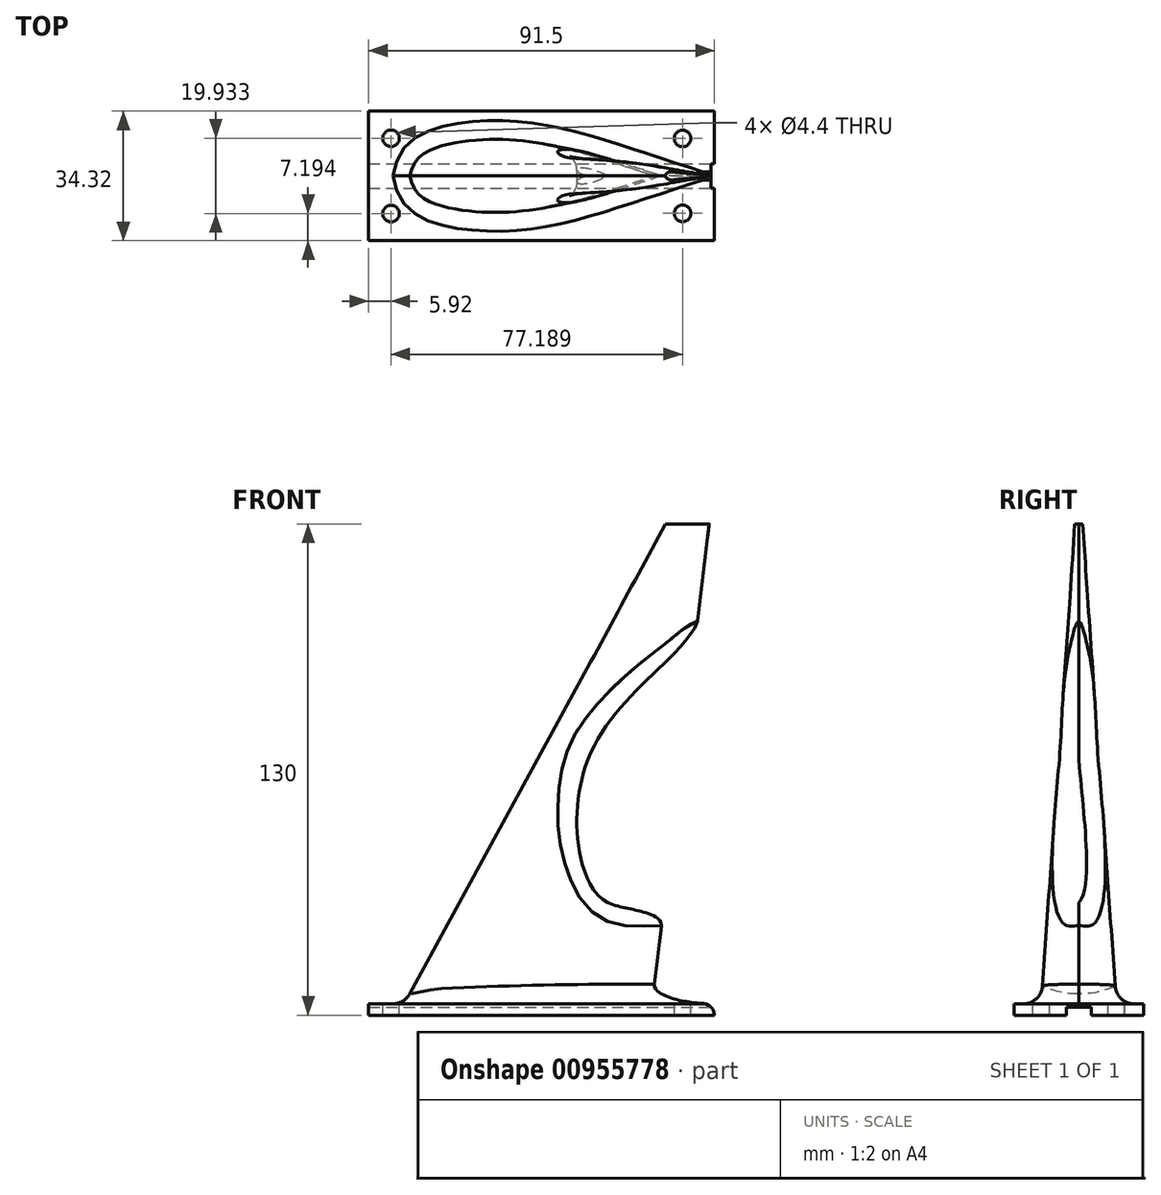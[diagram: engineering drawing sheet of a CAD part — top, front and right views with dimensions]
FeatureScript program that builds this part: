
annotation { "Feature Type Name" : "Feature", "Feature Type Description" : "" }
export const myFeature = defineFeature(function(context is Context, id is Id, definition is map)
    precondition{}
    {
        {
            var Q0;
            Q0=qCreatedBy(makeId("Top.planeOp"),FACE);
            var sketch = newSketch(context, id + "F0", { "sketchPlane" : qUnion([Q0])});
            skLineSegment(sketch, "E0", {"start": v(-28.36, 0) * mm, "end": v(38.49, 0) * mm});
            skFitSpline(sketch, "E1", {"points": [v(-28.36, 0) * mm, v(-22.92, 7.34) * mm, v(0, 10) * mm, v(38.49, 0) * mm], "startDerivative": vector(11.6, 54.73) * mm, "endDerivative": vector(109.69, -35.66) * mm});
            skFitSpline(sketch, "E2.MirrorCS", {"points": [v(-28.36, 0) * mm, v(-22.92, -7.34) * mm, v(0, -10) * mm, v(38.49, 0) * mm], "startDerivative": vector(11.6, -54.73) * mm, "endDerivative": vector(109.69, 35.66) * mm});
            skSolve(sketch);
        }
        {
            var Q0;
            Q0=qCreatedBy(makeId("Top.planeOp"),FACE);
            cPlane(context, id + "F1", {"entities" : qUnion([Q0]), "cplaneType" : CPlaneType.OFFSET, "offset" : 130 * mm, "width" : 150 * mm, "height" : 150 * mm});
        }
        {
            var Q0;
            Q0=qCreatedBy(id+"F1.planeOp",FACE);
            var sketch = newSketch(context, id + "F2", { "sketchPlane" : qUnion([Q0])});
            skFitSpline(sketch, "E3", {"points": [v(43.22, 0.93) * mm, v(45.42, 0.93) * mm, v(54, 0) * mm, v(42.5, 0) * mm, v(43.22, 0.93) * mm]});
            skLineSegment(sketch, "E4", {"start": v(42.5, 0) * mm, "end": v(54, 0) * mm});
            skFitSpline(sketch, "E5.MirrorCS", {"points": [v(43.22, -0.93) * mm, v(45.42, -0.93) * mm, v(54, 0) * mm, v(42.5, 0) * mm, v(43.22, -0.93) * mm]});
            skSolve(sketch);
        }
        {
            var Q0;
            Q0=qSketchRegion(id+"F2",true);
            var Q1;
            Q1=qSketchRegion(id+"F0",true);
            loft(context, id + "F3", {"sheetProfilesArray" : [{ "sheetProfileEntities" : qUnion([Q0]) }, { "sheetProfileEntities" : qUnion([Q1]) }]});
        }
        {
            var Q0;
            Q0=makeQuery(id+"F0.imprint","IMPRINT",FACE,{"disambiguationData":[TD([[makeQuery(id+"F0.imprint","IMPRINT",EDGE,{"derivedFrom":sQuery(id+"F0.wireOp",EDGE,"E0")}),1.0]])]});
            var sketch = newSketch(context, id + "F4", { "sketchPlane" : qUnion([Q0])});
            skLineSegment(sketch, "E6.bottom", {"start": v(-44.66, -14.97) * mm, "end": v(55.34, -14.97) * mm});
            skLineSegment(sketch, "E6.top", {"start": v(-44.66, 15.03) * mm, "end": v(55.34, 15.03) * mm});
            skLineSegment(sketch, "E6.left", {"start": v(-44.66, -14.97) * mm, "end": v(-44.66, 15.03) * mm});
            skLineSegment(sketch, "E6.right", {"start": v(55.34, -14.97) * mm, "end": v(55.34, 15.03) * mm});
            skLineSegment(sketch, "E7", {"start": v(-44.66, 0.03) * mm, "end": v(55.34, 0.03) * mm, "construction": true});
            skLineSegment(sketch, "E8", {"start": v(5.34, -14.97) * mm, "end": v(5.34, 15.03) * mm, "construction": true});
            skSolve(sketch);
        }
        {
            var Q0;
            Q0=makeQuery(id+"F6.boolean.opBoolean","MERGE",FACE,{"derivedFrom":[makeQuery(id+"F3.opLoft","CAP_FACE",FACE,{"disambiguationData":[OSD([makeQuery(id+"F0.imprint","IMPRINT",FACE,{"disambiguationData":[TD([[makeQuery(id+"F0.imprint","IMPRINT",EDGE,{"derivedFrom":sQuery(id+"F0.wireOp",EDGE,"E0")}),1.0]])]})])],"isStart":true}),makeQuery(id+"F6.opExtrude","CAP_FACE",FACE,{"disambiguationData":[OSD([sQuery(id+"F4.wireOp",EDGE,"E6.bottom"),sQuery(id+"F4.wireOp",EDGE,"E6.top"),sQuery(id+"F4.wireOp",EDGE,"E6.left"),sQuery(id+"F4.wireOp",EDGE,"E6.right")])],"isStart":true})]});
            var sketch = newSketch(context, id + "F5", { "sketchPlane" : qUnion([Q0])});
            skLineSegment(sketch, "E9.bottom", {"start": v(-44.68, 12) * mm, "end": v(-29.68, 12) * mm});
            skLineSegment(sketch, "E9.top", {"start": v(-44.68, 20) * mm, "end": v(-29.68, 20) * mm});
            skLineSegment(sketch, "E9.left", {"start": v(-44.68, 12) * mm, "end": v(-44.68, 20) * mm});
            skLineSegment(sketch, "E9.right", {"start": v(-29.68, 12) * mm, "end": v(-29.68, 20) * mm});
            skLineSegment(sketch, "E10.bottom", {"start": v(-44.68, -12) * mm, "end": v(-29.68, -12) * mm});
            skLineSegment(sketch, "E10.top", {"start": v(-44.68, -20) * mm, "end": v(-29.68, -20) * mm});
            skLineSegment(sketch, "E10.left", {"start": v(-44.68, -12) * mm, "end": v(-44.68, -20) * mm});
            skLineSegment(sketch, "E10.right", {"start": v(-29.68, -12) * mm, "end": v(-29.68, -20) * mm});
            skLineSegment(sketch, "E11", {"start": v(-29.68, 12) * mm, "end": v(-29.68, -12) * mm, "construction": true});
            skLineSegment(sketch, "E12.bottom", {"start": v(55.32, 12) * mm, "end": v(40.32, 12) * mm});
            skLineSegment(sketch, "E12.top", {"start": v(55.32, 20) * mm, "end": v(40.32, 20) * mm});
            skLineSegment(sketch, "E12.left", {"start": v(55.32, 12) * mm, "end": v(55.32, 20) * mm});
            skLineSegment(sketch, "E12.right", {"start": v(40.32, 12) * mm, "end": v(40.32, 20) * mm});
            skLineSegment(sketch, "E13.bottom", {"start": v(55.32, -12) * mm, "end": v(40.32, -12) * mm});
            skLineSegment(sketch, "E13.top", {"start": v(55.32, -20) * mm, "end": v(40.32, -20) * mm});
            skLineSegment(sketch, "E13.left", {"start": v(55.32, -12) * mm, "end": v(55.32, -20) * mm});
            skLineSegment(sketch, "E13.right", {"start": v(40.32, -12) * mm, "end": v(40.32, -20) * mm});
            skLineSegment(sketch, "E14", {"start": v(-37.18, 20) * mm, "end": v(-37.18, -20) * mm, "construction": true});
            skLineSegment(sketch, "E15", {"start": v(-44.68, 16) * mm, "end": v(40.32, 16) * mm, "construction": true});
            skLineSegment(sketch, "E16", {"start": v(-44.68, -16) * mm, "end": v(40.32, -16) * mm, "construction": true});
            skCircle(sketch, "E17", {"center": v(-37.18, 16) * mm, "radius": 2.2 * mm});
            skCircle(sketch, "E18", {"center": v(-37.18, -16) * mm, "radius": 2.2 * mm});
            skLineSegment(sketch, "E19", {"start": v(47.82, 20) * mm, "end": v(47.82, -20) * mm, "construction": true});
            skLineSegment(sketch, "E20", {"start": v(40.32, 16) * mm, "end": v(55.32, 16) * mm, "construction": true});
            skLineSegment(sketch, "E21", {"start": v(40.32, -16) * mm, "end": v(55.32, -16) * mm, "construction": true});
            skCircle(sketch, "E22", {"center": v(47.82, 16) * mm, "radius": 2.2 * mm});
            skCircle(sketch, "E23", {"center": v(47.82, -16) * mm, "radius": 2.2 * mm});
            skLineSegment(sketch, "E24", {"start": v(0, 16) * mm, "end": v(0, -16) * mm, "construction": true});
            skSolve(sketch);
        }
        {
            var Q0;
            Q0=qSketchRegion(id+"F4",true);
            extrude(context, id + "F6", {"entities" : qUnion([Q0]), "operationType" : NewBodyOperationType.ADD, "depth" : 3 * mm, "offsetDistance" : 25 * mm});
        }
        {
            var Q0;
            Q0=makeQuery(id+"F6.opExtrude","SWEPT_FACE",FACE,{"disambiguationData":[OSD([sQuery(id+"F4.wireOp",EDGE,"E6.top")])]});
            extrude(context, id + "F7", {"entities" : qUnion([Q0]), "operationType" : NewBodyOperationType.ADD, "depth" : 4 * mm, "offsetDistance" : 25 * mm});
        }
        {
            var Q0;
            Q0 = qSketchRegion(id + "F5", true);
            extrude(context, id + "F8", {"entities" : qUnion([Q0]), "operationType" : NewBodyOperationType.ADD, "oppositeDirection" : true, "depth" : 3 * mm, "offsetDistance" : 25 * mm});
        }
        {
            var Q0;
            Q0=qCreatedBy(makeId("Front.planeOp"),FACE);
            var sketch = newSketch(context, id + "F9", { "sketchPlane" : qUnion([Q0])});
            skFitSpline(sketch, "E25", {"points": [v(55.49, 27.74) * mm, v(25.19, 31.12) * mm, v(21.87, 67.64) * mm, v(46.79, 96.34) * mm, v(53, 100.6) * mm, v(57.62, 78.59) * mm], "startDerivative": vector(-212.63, 46.22) * mm, "endDerivative": vector(-52.55, -266.58) * mm});
            skLineSegment(sketch, "E26", {"start": v(55.49, 27.74) * mm, "end": v(57.62, 78.59) * mm});
            skSolve(sketch);
        }
        {
            var Q0;
            Q0 = qSketchRegion(id + "F9", true);
            extrude(context, id + "F10", {"entities" : qUnion([Q0]), "operationType" : NewBodyOperationType.REMOVE, "depth" : 50 * mm, "offsetDistance" : 25 * mm});
        }
        {
            var Q0;
            Q0 = qSketchRegion(id + "F9", true);
            extrude(context, id + "F11", {"entities" : qUnion([Q0]), "operationType" : NewBodyOperationType.REMOVE, "oppositeDirection" : true, "depth" : 25 * mm, "offsetDistance" : 25 * mm});
        }
        {
            var Q0;
            Q0=makeQuery(id+"F6.opExtrude","SWEPT_FACE",FACE,{"disambiguationData":[OSD([sQuery(id+"F4.wireOp",EDGE,"E6.bottom")])]});
            extrude(context, id + "F12", {"entities" : qUnion([Q0]), "operationType" : NewBodyOperationType.ADD, "depth" : 4 * mm, "offsetDistance" : 25 * mm});
        }
        {
            var Q0;
            {var subQ0=sQuery(id+"F2.wireOp",EDGE,"E5.MirrorCS");var subQ1=sQuery(id+"F2.wireOp",EDGE,"E4");var subQ2=sQuery(id+"F2.wireOp",EDGE,"E3");var subQ3=sQuery(id+"F0.wireOp",EDGE,"E2.MirrorCS");var subQ4=sQuery(id+"F0.wireOp",EDGE,"E1");var subQ5=sQuery(id+"F0.wireOp",EDGE,"E0");Q0=makeQuery(id+"F10.boolean.opBoolean","INTERSECT",EDGE,{"derivedFrom":[makeQuery(id+"F3.opLoft","SWEPT_FACE",FACE,{"disambiguationData":[OSD([subQ5,subQ4,subQ3,subQ2,subQ1,subQ0]),TDD([makeQuery(id+"F0.imprint","INTERSECT",VERTEX,{"disambiguationData":[OD(0.0)],"derivedFrom":[subQ5,subQ4,subQ3]}),makeQuery(id+"F0.imprint","INTERSECT",VERTEX,{"disambiguationData":[OD(1.0)],"derivedFrom":[subQ5,subQ4,subQ3]}),makeQuery(id+"F0.imprint","IMPRINT",EDGE,{"derivedFrom":subQ3}),makeQuery(id+"F2.imprint","INTERSECT",VERTEX,{"disambiguationData":[OD(0.0)],"derivedFrom":[subQ2,subQ1,subQ0]}),makeQuery(id+"F2.imprint","INTERSECT",VERTEX,{"disambiguationData":[OD(1.0)],"derivedFrom":[subQ2,subQ1,subQ0]}),makeQuery(id+"F2.imprint","IMPRINT",EDGE,{"derivedFrom":subQ0})])]}),makeQuery(id+"F10.opExtrude","SWEPT_FACE",FACE,{"disambiguationData":[OSD([sQuery(id+"F9.wireOp",EDGE,"E25")])]})]});}
            var Q1;
            {var subQ0=sQuery(id+"F2.wireOp",EDGE,"E3");var subQ1=sQuery(id+"F2.wireOp",EDGE,"E5.MirrorCS");var subQ2=sQuery(id+"F2.wireOp",EDGE,"E4");var subQ3=sQuery(id+"F0.wireOp",EDGE,"E1");var subQ4=sQuery(id+"F0.wireOp",EDGE,"E2.MirrorCS");var subQ5=sQuery(id+"F0.wireOp",EDGE,"E0");Q1=makeQuery(id+"F11.boolean.opBoolean","INTERSECT",EDGE,{"derivedFrom":[makeQuery(id+"F3.opLoft","SWEPT_FACE",FACE,{"disambiguationData":[OSD([subQ5,subQ3,subQ4,subQ0,subQ2,subQ1]),TDD([makeQuery(id+"F0.imprint","INTERSECT",VERTEX,{"disambiguationData":[OD(0.0)],"derivedFrom":[subQ5,subQ3,subQ4]}),makeQuery(id+"F0.imprint","INTERSECT",VERTEX,{"disambiguationData":[OD(1.0)],"derivedFrom":[subQ5,subQ3,subQ4]}),makeQuery(id+"F0.imprint","IMPRINT",EDGE,{"derivedFrom":subQ3}),makeQuery(id+"F2.imprint","INTERSECT",VERTEX,{"disambiguationData":[OD(0.0)],"derivedFrom":[subQ0,subQ2,subQ1]}),makeQuery(id+"F2.imprint","INTERSECT",VERTEX,{"disambiguationData":[OD(1.0)],"derivedFrom":[subQ0,subQ2,subQ1]}),makeQuery(id+"F2.imprint","IMPRINT",EDGE,{"derivedFrom":subQ0})])]}),makeQuery(id+"F11.opExtrude","SWEPT_FACE",FACE,{"disambiguationData":[OSD([sQuery(id+"F9.wireOp",EDGE,"E25")])]})]});}
            fillet(context, id + "F13", {"entities" : qUnion([Q0, Q1]), "radius" : 5 * mm, "tangentPropagation" : true, "allowEdgeOverflow" : false});
        }
        {
            var Q0;
            {var subQ0=sQuery(id+"F2.wireOp",EDGE,"E3");var subQ1=sQuery(id+"F2.wireOp",EDGE,"E5.MirrorCS");var subQ2=sQuery(id+"F2.wireOp",EDGE,"E4");var subQ3=sQuery(id+"F0.wireOp",EDGE,"E1");var subQ4=sQuery(id+"F0.wireOp",EDGE,"E2.MirrorCS");var subQ5=sQuery(id+"F0.wireOp",EDGE,"E0");Q0=makeQuery(id+"F6.boolean.opBoolean","INTERSECT",EDGE,{"derivedFrom":[makeQuery(id+"F3.opLoft","SWEPT_FACE",FACE,{"disambiguationData":[OSD([subQ5,subQ3,subQ4,subQ0,subQ2,subQ1]),TDD([makeQuery(id+"F0.imprint","INTERSECT",VERTEX,{"disambiguationData":[OD(0.0)],"derivedFrom":[subQ5,subQ3,subQ4]}),makeQuery(id+"F0.imprint","INTERSECT",VERTEX,{"disambiguationData":[OD(1.0)],"derivedFrom":[subQ5,subQ3,subQ4]}),makeQuery(id+"F0.imprint","IMPRINT",EDGE,{"derivedFrom":subQ3}),makeQuery(id+"F2.imprint","INTERSECT",VERTEX,{"disambiguationData":[OD(0.0)],"derivedFrom":[subQ0,subQ2,subQ1]}),makeQuery(id+"F2.imprint","INTERSECT",VERTEX,{"disambiguationData":[OD(1.0)],"derivedFrom":[subQ0,subQ2,subQ1]}),makeQuery(id+"F2.imprint","IMPRINT",EDGE,{"derivedFrom":subQ0})])]}),makeQuery(id+"F6.opExtrude","CAP_FACE",FACE,{"disambiguationData":[OSD([sQuery(id+"F4.wireOp",EDGE,"E6.bottom"),sQuery(id+"F4.wireOp",EDGE,"E6.top"),sQuery(id+"F4.wireOp",EDGE,"E6.left"),sQuery(id+"F4.wireOp",EDGE,"E6.right")])],"isStart":false})]});}
            var Q1;
            {var subQ0=sQuery(id+"F2.wireOp",EDGE,"E5.MirrorCS");var subQ1=sQuery(id+"F2.wireOp",EDGE,"E4");var subQ2=sQuery(id+"F2.wireOp",EDGE,"E3");var subQ3=sQuery(id+"F0.wireOp",EDGE,"E2.MirrorCS");var subQ4=sQuery(id+"F0.wireOp",EDGE,"E1");var subQ5=sQuery(id+"F0.wireOp",EDGE,"E0");Q1=makeQuery(id+"F6.boolean.opBoolean","INTERSECT",EDGE,{"derivedFrom":[makeQuery(id+"F3.opLoft","SWEPT_FACE",FACE,{"disambiguationData":[OSD([subQ5,subQ4,subQ3,subQ2,subQ1,subQ0]),TDD([makeQuery(id+"F0.imprint","INTERSECT",VERTEX,{"disambiguationData":[OD(0.0)],"derivedFrom":[subQ5,subQ4,subQ3]}),makeQuery(id+"F0.imprint","INTERSECT",VERTEX,{"disambiguationData":[OD(1.0)],"derivedFrom":[subQ5,subQ4,subQ3]}),makeQuery(id+"F0.imprint","IMPRINT",EDGE,{"derivedFrom":subQ3}),makeQuery(id+"F2.imprint","INTERSECT",VERTEX,{"disambiguationData":[OD(0.0)],"derivedFrom":[subQ2,subQ1,subQ0]}),makeQuery(id+"F2.imprint","INTERSECT",VERTEX,{"disambiguationData":[OD(1.0)],"derivedFrom":[subQ2,subQ1,subQ0]}),makeQuery(id+"F2.imprint","IMPRINT",EDGE,{"derivedFrom":subQ0})])]}),makeQuery(id+"F6.opExtrude","CAP_FACE",FACE,{"disambiguationData":[OSD([sQuery(id+"F4.wireOp",EDGE,"E6.bottom"),sQuery(id+"F4.wireOp",EDGE,"E6.top"),sQuery(id+"F4.wireOp",EDGE,"E6.left"),sQuery(id+"F4.wireOp",EDGE,"E6.right")])],"isStart":false})]});}
            fillet(context, id + "F14", {"entities" : qUnion([Q0, Q1]), "radius" : 5 * mm, "tangentPropagation" : true, "allowEdgeOverflow" : false});
        }
        {
            var Q0;
            Q0=makeQuery(id+"F12.boolean.opBoolean","INTERSECT",EDGE,{"derivedFrom":[makeQuery(id+"F8.opExtrude","SWEPT_FACE",FACE,{"disambiguationData":[OSD([sQuery(id+"F5.wireOp",EDGE,"E9.right")])]}),makeQuery(id+"F12.opExtrude","CAP_FACE",FACE,{"disambiguationData":[OSD([sQuery(id+"F4.wireOp",EDGE,"E6.bottom")])],"isStart":false})]});
            var Q1;
            Q1=makeQuery(id+"F12.boolean.opBoolean","INTERSECT",EDGE,{"derivedFrom":[makeQuery(id+"F8.opExtrude","SWEPT_FACE",FACE,{"disambiguationData":[OSD([sQuery(id+"F5.wireOp",EDGE,"E12.right")])]}),makeQuery(id+"F12.opExtrude","CAP_FACE",FACE,{"disambiguationData":[OSD([sQuery(id+"F4.wireOp",EDGE,"E6.bottom")])],"isStart":false})]});
            var Q2;
            Q2=makeQuery(id+"F8.boolean.opBoolean","INTERSECT",EDGE,{"derivedFrom":[makeQuery(id+"F7.opExtrude","CAP_FACE",FACE,{"disambiguationData":[OSD([sQuery(id+"F4.wireOp",EDGE,"E6.top")])],"isStart":false}),makeQuery(id+"F8.opExtrude","SWEPT_FACE",FACE,{"disambiguationData":[OSD([sQuery(id+"F5.wireOp",EDGE,"E13.right")])]})]});
            var Q3;
            Q3=makeQuery(id+"F8.boolean.opBoolean","INTERSECT",EDGE,{"derivedFrom":[makeQuery(id+"F7.opExtrude","CAP_FACE",FACE,{"disambiguationData":[OSD([sQuery(id+"F4.wireOp",EDGE,"E6.top")])],"isStart":false}),makeQuery(id+"F8.opExtrude","SWEPT_FACE",FACE,{"disambiguationData":[OSD([sQuery(id+"F5.wireOp",EDGE,"E10.right")])]})]});
            fillet(context, id + "F15", {"entities" : qUnion([Q0, Q1, Q2, Q3]), "radius" : 5 * mm, "tangentPropagation" : true, "allowEdgeOverflow" : false});
        }
        {
            var Q0;
            {var subQ0=sQuery(id+"F5.wireOp",EDGE,"E17");var subQ1=sQuery(id+"F5.wireOp",EDGE,"E9.right");var subQ2=makeQuery(id+"F8.opExtrude","CAP_FACE",FACE,{"disambiguationData":[OSD([sQuery(id+"F5.wireOp",EDGE,"E9.bottom"),sQuery(id+"F5.wireOp",EDGE,"E9.top"),sQuery(id+"F5.wireOp",EDGE,"E9.left"),subQ1,subQ0])],"isStart":false});var subQ3=sQuery(id+"F4.wireOp",EDGE,"E6.right");var subQ4=sQuery(id+"F4.wireOp",EDGE,"E6.top");var subQ5=sQuery(id+"F4.wireOp",EDGE,"E6.bottom");var subQ6=makeQuery(id+"F6.opExtrude","CAP_FACE",FACE,{"disambiguationData":[OSD([subQ5,subQ4,sQuery(id+"F4.wireOp",EDGE,"E6.left"),subQ3])],"isStart":false});var subQ7=makeQuery(id+"F7.opExtrude","SWEPT_FACE",FACE,{"disambiguationData":[OSD([subQ4]),TDD([makeQuery(id+"F6.opExtrude","CAP_EDGE",EDGE,{"disambiguationData":[OSD([subQ4])],"isStart":false})])]});var subQ9=makeQuery(id+"F8.opExtrude","CAP_FACE",FACE,{"disambiguationData":[OSD([sQuery(id+"F5.wireOp",EDGE,"E13.bottom"),sQuery(id+"F5.wireOp",EDGE,"E13.top"),sQuery(id+"F5.wireOp",EDGE,"E13.left"),sQuery(id+"F5.wireOp",EDGE,"E13.right"),sQuery(id+"F5.wireOp",EDGE,"E23")])],"isStart":false});var subQ10=makeQuery(id+"F8.opExtrude","CAP_FACE",FACE,{"disambiguationData":[OSD([sQuery(id+"F5.wireOp",EDGE,"E10.bottom"),sQuery(id+"F5.wireOp",EDGE,"E10.top"),sQuery(id+"F5.wireOp",EDGE,"E10.left"),sQuery(id+"F5.wireOp",EDGE,"E10.right"),sQuery(id+"F5.wireOp",EDGE,"E18")])],"isStart":false});var subQ11=sQuery(id+"F5.wireOp",EDGE,"E22");var subQ12=sQuery(id+"F5.wireOp",EDGE,"E12.right");var subQ13=sQuery(id+"F5.wireOp",EDGE,"E12.left");var subQ14=makeQuery(id+"F8.opExtrude","CAP_FACE",FACE,{"disambiguationData":[OSD([sQuery(id+"F5.wireOp",EDGE,"E12.bottom"),sQuery(id+"F5.wireOp",EDGE,"E12.top"),subQ13,subQ12,subQ11])],"isStart":false});var subQ15=makeQuery(id+"F6.opExtrude","CAP_EDGE",EDGE,{"disambiguationData":[OSD([subQ5])],"isStart":false});Q0=makeQuery(id+"F12.boolean.opBoolean","MERGE",FACE,{"derivedFrom":[makeQuery(id+"F8.boolean.opBoolean","MERGE",FACE,{"derivedFrom":[makeQuery(id+"F7.boolean.opBoolean","MERGE",FACE,{"derivedFrom":[subQ6,subQ7]}),subQ2,subQ10,subQ14,subQ9]}),makeQuery(id+"F12.opExtrude","SWEPT_FACE",FACE,{"disambiguationData":[OSD([subQ5]),TDD([makeQuery(id+"F8.boolean.opBoolean","SPLIT",EDGE,{"disambiguationData":[TD([makeQuery(id+"F6.opExtrude","SWEPT_FACE",FACE,{"disambiguationData":[OSD([subQ3])]})])],"derivedFrom":subQ15})])]}),makeQuery(id+"F12.opExtrude","SWEPT_FACE",FACE,{"disambiguationData":[OSD([subQ5]),TDD([makeQuery(id+"F8.boolean.opBoolean","SPLIT",EDGE,{"disambiguationData":[TD([makeQuery(id+"F8.opExtrude","SWEPT_FACE",FACE,{"disambiguationData":[OSD([subQ1])]})])],"derivedFrom":subQ15})])]}),makeQuery(id+"F12.opExtrude","SWEPT_FACE",FACE,{"disambiguationData":[OSD([subQ5]),TDD([makeQuery(id+"F8.boolean.opBoolean","SPLIT",EDGE,{"disambiguationData":[TD([makeQuery(id+"F8.opExtrude","SWEPT_FACE",FACE,{"disambiguationData":[OSD([subQ0])]})])],"derivedFrom":subQ15})])]}),makeQuery(id+"F12.opExtrude","SWEPT_FACE",FACE,{"disambiguationData":[OSD([subQ5]),TDD([makeQuery(id+"F8.boolean.opBoolean","SPLIT",EDGE,{"disambiguationData":[TD([makeQuery(id+"F8.opExtrude","SWEPT_FACE",FACE,{"disambiguationData":[OSD([subQ11])]})])],"derivedFrom":subQ15})])]})]});}
            var sketch = newSketch(context, id + "F16", { "sketchPlane" : qUnion([Q0])});
            skLineSegment(sketch, "E27.bottom", {"start": v(-44.68, 20) * mm, "end": v(55.32, 20) * mm});
            skLineSegment(sketch, "E27.top", {"start": v(-44.68, -20) * mm, "end": v(55.32, -20) * mm});
            skLineSegment(sketch, "E27.left", {"start": v(-44.68, 20) * mm, "end": v(-44.68, -20) * mm});
            skLineSegment(sketch, "E27.right", {"start": v(55.32, 20) * mm, "end": v(55.32, -20) * mm});
            skSolve(sketch);
        }
        {
            var Q0;
            Q0 = qSketchRegion(id + "F16", true);
            var Q1;
            {var subQ0=sQuery(id+"F4.wireOp",EDGE,"E6.top");var subQ1=makeQuery(id+"F7.opExtrude","SWEPT_FACE",FACE,{"disambiguationData":[OSD([subQ0]),TDD([makeQuery(id+"F6.opExtrude","CAP_EDGE",EDGE,{"disambiguationData":[OSD([subQ0])],"isStart":true})])]});var subQ2=makeQuery(id+"F8.opExtrude","CAP_FACE",FACE,{"disambiguationData":[OSD([sQuery(id+"F5.wireOp",EDGE,"E13.bottom"),sQuery(id+"F5.wireOp",EDGE,"E13.top"),sQuery(id+"F5.wireOp",EDGE,"E13.left"),sQuery(id+"F5.wireOp",EDGE,"E13.right"),sQuery(id+"F5.wireOp",EDGE,"E23")])],"isStart":true});var subQ3=sQuery(id+"F4.wireOp",EDGE,"E6.right");var subQ4=sQuery(id+"F4.wireOp",EDGE,"E6.bottom");var subQ5=makeQuery(id+"F6.opExtrude","CAP_FACE",FACE,{"disambiguationData":[OSD([subQ4,subQ0,sQuery(id+"F4.wireOp",EDGE,"E6.left"),subQ3])],"isStart":true});var subQ7=makeQuery(id+"F0.imprint","IMPRINT",EDGE,{"derivedFrom":sQuery(id+"F0.wireOp",EDGE,"E0")});var subQ8=makeQuery(id+"F3.opLoft","CAP_FACE",FACE,{"disambiguationData":[OSD([makeQuery(id+"F0.imprint","IMPRINT",FACE,{"disambiguationData":[TD([[subQ7,1.0]])]}),makeQuery(id+"F0.imprint","IMPRINT",FACE,{"disambiguationData":[TD([[subQ7,-1.0]])]})])],"isStart":true});var subQ9=sQuery(id+"F5.wireOp",EDGE,"E22");var subQ10=sQuery(id+"F5.wireOp",EDGE,"E12.right");var subQ11=sQuery(id+"F5.wireOp",EDGE,"E12.left");var subQ12=makeQuery(id+"F8.opExtrude","CAP_FACE",FACE,{"disambiguationData":[OSD([sQuery(id+"F5.wireOp",EDGE,"E12.bottom"),sQuery(id+"F5.wireOp",EDGE,"E12.top"),subQ11,subQ10,subQ9])],"isStart":true});var subQ13=sQuery(id+"F5.wireOp",EDGE,"E17");var subQ14=sQuery(id+"F5.wireOp",EDGE,"E9.right");var subQ15=makeQuery(id+"F8.opExtrude","CAP_FACE",FACE,{"disambiguationData":[OSD([sQuery(id+"F5.wireOp",EDGE,"E9.bottom"),sQuery(id+"F5.wireOp",EDGE,"E9.top"),sQuery(id+"F5.wireOp",EDGE,"E9.left"),subQ14,subQ13])],"isStart":true});var subQ16=makeQuery(id+"F8.opExtrude","CAP_FACE",FACE,{"disambiguationData":[OSD([sQuery(id+"F5.wireOp",EDGE,"E10.bottom"),sQuery(id+"F5.wireOp",EDGE,"E10.top"),sQuery(id+"F5.wireOp",EDGE,"E10.left"),sQuery(id+"F5.wireOp",EDGE,"E10.right"),sQuery(id+"F5.wireOp",EDGE,"E18")])],"isStart":true});var subQ17=makeQuery(id+"F6.opExtrude","CAP_EDGE",EDGE,{"disambiguationData":[OSD([subQ4])],"isStart":true});Q1=makeQuery(id+"F12.boolean.opBoolean","MERGE",FACE,{"derivedFrom":[makeQuery(id+"F8.boolean.opBoolean","MERGE",FACE,{"derivedFrom":[makeQuery(id+"F7.boolean.opBoolean","MERGE",FACE,{"derivedFrom":[makeQuery(id+"F6.boolean.opBoolean","MERGE",FACE,{"derivedFrom":[subQ8,subQ5]}),subQ1]}),subQ15,subQ16,subQ12,subQ2]}),makeQuery(id+"F12.opExtrude","SWEPT_FACE",FACE,{"disambiguationData":[OSD([subQ4]),TDD([makeQuery(id+"F8.boolean.opBoolean","SPLIT",EDGE,{"disambiguationData":[TD([makeQuery(id+"F6.opExtrude","SWEPT_FACE",FACE,{"disambiguationData":[OSD([subQ3])]})])],"derivedFrom":subQ17})])]}),makeQuery(id+"F12.opExtrude","SWEPT_FACE",FACE,{"disambiguationData":[OSD([subQ4]),TDD([makeQuery(id+"F8.boolean.opBoolean","SPLIT",EDGE,{"disambiguationData":[TD([makeQuery(id+"F8.opExtrude","SWEPT_FACE",FACE,{"disambiguationData":[OSD([subQ14])]})])],"derivedFrom":subQ17})])]}),makeQuery(id+"F12.opExtrude","SWEPT_FACE",FACE,{"disambiguationData":[OSD([subQ4]),TDD([makeQuery(id+"F8.boolean.opBoolean","SPLIT",EDGE,{"disambiguationData":[TD([makeQuery(id+"F8.opExtrude","SWEPT_FACE",FACE,{"disambiguationData":[OSD([subQ13])]})])],"derivedFrom":subQ17})])]}),makeQuery(id+"F12.opExtrude","SWEPT_FACE",FACE,{"disambiguationData":[OSD([subQ4]),TDD([makeQuery(id+"F8.boolean.opBoolean","SPLIT",EDGE,{"disambiguationData":[TD([makeQuery(id+"F8.opExtrude","SWEPT_FACE",FACE,{"disambiguationData":[OSD([subQ9])]})])],"derivedFrom":subQ17})])]})]});}
            extrude(context, id + "F17", {"entities" : qUnion([Q0]), "operationType" : NewBodyOperationType.ADD, "endBound" : BoundingType.UP_TO_SURFACE, "oppositeDirection" : true, "depth" : 25 * mm, "endBoundEntityFace" : qUnion([Q1]), "offsetDistance" : 25 * mm});
        }
        {
            var Q0;
            {var subQ0=sQuery(id+"F5.wireOp",EDGE,"E17");var subQ1=sQuery(id+"F5.wireOp",EDGE,"E9.right");var subQ2=makeQuery(id+"F8.opExtrude","CAP_FACE",FACE,{"disambiguationData":[OSD([sQuery(id+"F5.wireOp",EDGE,"E9.bottom"),sQuery(id+"F5.wireOp",EDGE,"E9.top"),sQuery(id+"F5.wireOp",EDGE,"E9.left"),subQ1,subQ0])],"isStart":false});var subQ3=sQuery(id+"F4.wireOp",EDGE,"E6.right");var subQ4=sQuery(id+"F4.wireOp",EDGE,"E6.top");var subQ5=sQuery(id+"F4.wireOp",EDGE,"E6.bottom");var subQ6=makeQuery(id+"F6.opExtrude","CAP_FACE",FACE,{"disambiguationData":[OSD([subQ5,subQ4,sQuery(id+"F4.wireOp",EDGE,"E6.left"),subQ3])],"isStart":false});var subQ7=makeQuery(id+"F7.opExtrude","SWEPT_FACE",FACE,{"disambiguationData":[OSD([subQ4]),TDD([makeQuery(id+"F6.opExtrude","CAP_EDGE",EDGE,{"disambiguationData":[OSD([subQ4])],"isStart":false})])]});var subQ9=makeQuery(id+"F8.opExtrude","CAP_FACE",FACE,{"disambiguationData":[OSD([sQuery(id+"F5.wireOp",EDGE,"E13.bottom"),sQuery(id+"F5.wireOp",EDGE,"E13.top"),sQuery(id+"F5.wireOp",EDGE,"E13.left"),sQuery(id+"F5.wireOp",EDGE,"E13.right"),sQuery(id+"F5.wireOp",EDGE,"E23")])],"isStart":false});var subQ10=makeQuery(id+"F8.opExtrude","CAP_FACE",FACE,{"disambiguationData":[OSD([sQuery(id+"F5.wireOp",EDGE,"E10.bottom"),sQuery(id+"F5.wireOp",EDGE,"E10.top"),sQuery(id+"F5.wireOp",EDGE,"E10.left"),sQuery(id+"F5.wireOp",EDGE,"E10.right"),sQuery(id+"F5.wireOp",EDGE,"E18")])],"isStart":false});var subQ11=sQuery(id+"F5.wireOp",EDGE,"E22");var subQ12=sQuery(id+"F5.wireOp",EDGE,"E12.right");var subQ13=sQuery(id+"F5.wireOp",EDGE,"E12.left");var subQ14=makeQuery(id+"F8.opExtrude","CAP_FACE",FACE,{"disambiguationData":[OSD([sQuery(id+"F5.wireOp",EDGE,"E12.bottom"),sQuery(id+"F5.wireOp",EDGE,"E12.top"),subQ13,subQ12,subQ11])],"isStart":false});var subQ15=makeQuery(id+"F6.opExtrude","CAP_EDGE",EDGE,{"disambiguationData":[OSD([subQ5])],"isStart":false});Q0=makeQuery(id+"F17.boolean.opBoolean","MERGE",FACE,{"derivedFrom":[makeQuery(id+"F12.boolean.opBoolean","MERGE",FACE,{"derivedFrom":[makeQuery(id+"F8.boolean.opBoolean","MERGE",FACE,{"derivedFrom":[makeQuery(id+"F7.boolean.opBoolean","MERGE",FACE,{"derivedFrom":[subQ6,subQ7]}),subQ2,subQ10,subQ14,subQ9]}),makeQuery(id+"F12.opExtrude","SWEPT_FACE",FACE,{"disambiguationData":[OSD([subQ5]),TDD([makeQuery(id+"F8.boolean.opBoolean","SPLIT",EDGE,{"disambiguationData":[TD([makeQuery(id+"F6.opExtrude","SWEPT_FACE",FACE,{"disambiguationData":[OSD([subQ3])]})])],"derivedFrom":subQ15})])]}),makeQuery(id+"F12.opExtrude","SWEPT_FACE",FACE,{"disambiguationData":[OSD([subQ5]),TDD([makeQuery(id+"F8.boolean.opBoolean","SPLIT",EDGE,{"disambiguationData":[TD([makeQuery(id+"F8.opExtrude","SWEPT_FACE",FACE,{"disambiguationData":[OSD([subQ1])]})])],"derivedFrom":subQ15})])]}),makeQuery(id+"F12.opExtrude","SWEPT_FACE",FACE,{"disambiguationData":[OSD([subQ5]),TDD([makeQuery(id+"F8.boolean.opBoolean","SPLIT",EDGE,{"disambiguationData":[TD([makeQuery(id+"F8.opExtrude","SWEPT_FACE",FACE,{"disambiguationData":[OSD([subQ0])]})])],"derivedFrom":subQ15})])]}),makeQuery(id+"F12.opExtrude","SWEPT_FACE",FACE,{"disambiguationData":[OSD([subQ5]),TDD([makeQuery(id+"F8.boolean.opBoolean","SPLIT",EDGE,{"disambiguationData":[TD([makeQuery(id+"F8.opExtrude","SWEPT_FACE",FACE,{"disambiguationData":[OSD([subQ11])]})])],"derivedFrom":subQ15})])]})]}),makeQuery(id+"F17.opExtrude","CAP_FACE",FACE,{"disambiguationData":[OSD([sQuery(id+"F16.wireOp",EDGE,"E27.bottom"),sQuery(id+"F16.wireOp",EDGE,"E27.top"),sQuery(id+"F16.wireOp",EDGE,"E27.left"),sQuery(id+"F16.wireOp",EDGE,"E27.right")])],"isStart":true})]});}
            var sketch = newSketch(context, id + "F18", { "sketchPlane" : qUnion([Q0])});
            skLineSegment(sketch, "E28.bottom", {"start": v(55.34, 17.16) * mm, "end": v(-36.16, 17.16) * mm});
            skLineSegment(sketch, "E28.top", {"start": v(55.34, -17.16) * mm, "end": v(-36.16, -17.16) * mm});
            skLineSegment(sketch, "E28.left", {"start": v(55.34, 17.16) * mm, "end": v(55.34, -17.16) * mm});
            skLineSegment(sketch, "E28.right", {"start": v(-36.16, 17.16) * mm, "end": v(-36.16, -17.16) * mm});
            skLineSegment(sketch, "E29", {"start": v(-36.16, 0) * mm, "end": v(0, 0) * mm, "construction": true});
            skLineSegment(sketch, "E30.bottom", {"start": v(-66.77, 30.67) * mm, "end": v(66.77, 30.67) * mm});
            skLineSegment(sketch, "E30.top", {"start": v(-66.77, -30.67) * mm, "end": v(66.77, -30.67) * mm});
            skLineSegment(sketch, "E30.left", {"start": v(-66.77, 30.67) * mm, "end": v(-66.77, -30.67) * mm});
            skLineSegment(sketch, "E30.right", {"start": v(66.77, 30.67) * mm, "end": v(66.77, -30.67) * mm});
            skPoint(sketch, "E30.middle", {"position": v(0, 0) * mm});
            skSolve(sketch);
        }
        {
            var Q0;
            Q0 = qSketchRegion(id + "F18", true);
            extrude(context, id + "F19", {"entities" : qUnion([Q0]), "operationType" : NewBodyOperationType.REMOVE, "oppositeDirection" : true, "depth" : 25 * mm, "offsetDistance" : 25 * mm});
        }
        {
            var Q0;
            {var subQ0=sQuery(id+"F5.wireOp",EDGE,"E17");var subQ1=sQuery(id+"F5.wireOp",EDGE,"E9.right");var subQ2=makeQuery(id+"F8.opExtrude","CAP_FACE",FACE,{"disambiguationData":[OSD([sQuery(id+"F5.wireOp",EDGE,"E9.bottom"),sQuery(id+"F5.wireOp",EDGE,"E9.top"),sQuery(id+"F5.wireOp",EDGE,"E9.left"),subQ1,subQ0])],"isStart":false});var subQ3=sQuery(id+"F4.wireOp",EDGE,"E6.right");var subQ4=sQuery(id+"F4.wireOp",EDGE,"E6.top");var subQ5=sQuery(id+"F4.wireOp",EDGE,"E6.bottom");var subQ6=makeQuery(id+"F6.opExtrude","CAP_FACE",FACE,{"disambiguationData":[OSD([subQ5,subQ4,sQuery(id+"F4.wireOp",EDGE,"E6.left"),subQ3])],"isStart":false});var subQ7=makeQuery(id+"F7.opExtrude","SWEPT_FACE",FACE,{"disambiguationData":[OSD([subQ4]),TDD([makeQuery(id+"F6.opExtrude","CAP_EDGE",EDGE,{"disambiguationData":[OSD([subQ4])],"isStart":false})])]});var subQ9=makeQuery(id+"F8.opExtrude","CAP_FACE",FACE,{"disambiguationData":[OSD([sQuery(id+"F5.wireOp",EDGE,"E13.bottom"),sQuery(id+"F5.wireOp",EDGE,"E13.top"),sQuery(id+"F5.wireOp",EDGE,"E13.left"),sQuery(id+"F5.wireOp",EDGE,"E13.right"),sQuery(id+"F5.wireOp",EDGE,"E23")])],"isStart":false});var subQ10=makeQuery(id+"F8.opExtrude","CAP_FACE",FACE,{"disambiguationData":[OSD([sQuery(id+"F5.wireOp",EDGE,"E10.bottom"),sQuery(id+"F5.wireOp",EDGE,"E10.top"),sQuery(id+"F5.wireOp",EDGE,"E10.left"),sQuery(id+"F5.wireOp",EDGE,"E10.right"),sQuery(id+"F5.wireOp",EDGE,"E18")])],"isStart":false});var subQ11=sQuery(id+"F5.wireOp",EDGE,"E22");var subQ12=sQuery(id+"F5.wireOp",EDGE,"E12.right");var subQ13=sQuery(id+"F5.wireOp",EDGE,"E12.left");var subQ14=makeQuery(id+"F8.opExtrude","CAP_FACE",FACE,{"disambiguationData":[OSD([sQuery(id+"F5.wireOp",EDGE,"E12.bottom"),sQuery(id+"F5.wireOp",EDGE,"E12.top"),subQ13,subQ12,subQ11])],"isStart":false});var subQ15=makeQuery(id+"F6.opExtrude","CAP_EDGE",EDGE,{"disambiguationData":[OSD([subQ5])],"isStart":false});Q0=makeQuery(id+"F17.boolean.opBoolean","MERGE",FACE,{"derivedFrom":[makeQuery(id+"F12.boolean.opBoolean","MERGE",FACE,{"derivedFrom":[makeQuery(id+"F8.boolean.opBoolean","MERGE",FACE,{"derivedFrom":[makeQuery(id+"F7.boolean.opBoolean","MERGE",FACE,{"derivedFrom":[subQ6,subQ7]}),subQ2,subQ10,subQ14,subQ9]}),makeQuery(id+"F12.opExtrude","SWEPT_FACE",FACE,{"disambiguationData":[OSD([subQ5]),TDD([makeQuery(id+"F8.boolean.opBoolean","SPLIT",EDGE,{"disambiguationData":[TD([makeQuery(id+"F6.opExtrude","SWEPT_FACE",FACE,{"disambiguationData":[OSD([subQ3])]})])],"derivedFrom":subQ15})])]}),makeQuery(id+"F12.opExtrude","SWEPT_FACE",FACE,{"disambiguationData":[OSD([subQ5]),TDD([makeQuery(id+"F8.boolean.opBoolean","SPLIT",EDGE,{"disambiguationData":[TD([makeQuery(id+"F8.opExtrude","SWEPT_FACE",FACE,{"disambiguationData":[OSD([subQ1])]})])],"derivedFrom":subQ15})])]}),makeQuery(id+"F12.opExtrude","SWEPT_FACE",FACE,{"disambiguationData":[OSD([subQ5]),TDD([makeQuery(id+"F8.boolean.opBoolean","SPLIT",EDGE,{"disambiguationData":[TD([makeQuery(id+"F8.opExtrude","SWEPT_FACE",FACE,{"disambiguationData":[OSD([subQ0])]})])],"derivedFrom":subQ15})])]}),makeQuery(id+"F12.opExtrude","SWEPT_FACE",FACE,{"disambiguationData":[OSD([subQ5]),TDD([makeQuery(id+"F8.boolean.opBoolean","SPLIT",EDGE,{"disambiguationData":[TD([makeQuery(id+"F8.opExtrude","SWEPT_FACE",FACE,{"disambiguationData":[OSD([subQ11])]})])],"derivedFrom":subQ15})])]})]}),makeQuery(id+"F17.opExtrude","CAP_FACE",FACE,{"disambiguationData":[OSD([sQuery(id+"F16.wireOp",EDGE,"E27.bottom"),sQuery(id+"F16.wireOp",EDGE,"E27.top"),sQuery(id+"F16.wireOp",EDGE,"E27.left"),sQuery(id+"F16.wireOp",EDGE,"E27.right")])],"isStart":true})]});}
            var sketch = newSketch(context, id + "F20", { "sketchPlane" : qUnion([Q0])});
            skCircle(sketch, "E31", {"center": v(-30.24, 9.97) * mm, "radius": 2.2 * mm});
            skCircle(sketch, "E32", {"center": v(46.95, 9.92) * mm, "radius": 2.2 * mm});
            skLineSegment(sketch, "E33", {"start": v(-36.16, 0) * mm, "end": v(0, 0) * mm, "construction": true});
            skCircle(sketch, "E34.MirrorC", {"center": v(46.95, -9.92) * mm, "radius": 2.2 * mm});
            skCircle(sketch, "E35.MirrorC", {"center": v(-30.24, -9.97) * mm, "radius": 2.2 * mm});
            skSolve(sketch);
        }
        {
            var Q0;
            Q0 = qSketchRegion(id + "F20", true);
            extrude(context, id + "F21", {"entities" : qUnion([Q0]), "operationType" : NewBodyOperationType.REMOVE, "oppositeDirection" : true, "depth" : 25 * mm, "offsetDistance" : 25 * mm});
        }
        {
            var Q0;
            Q0=makeQuery(id+"F19.boolean.opBoolean","COPY",EDGE,{"derivedFrom":makeQuery(id+"F19.opExtrude","CAP_EDGE",EDGE,{"disambiguationData":[OSD([sQuery(id+"F18.wireOp",EDGE,"E28.bottom")])],"isStart":true})});
            var Q1;
            Q1=makeQuery(id+"F19.boolean.opBoolean","COPY",EDGE,{"derivedFrom":makeQuery(id+"F19.opExtrude","CAP_EDGE",EDGE,{"disambiguationData":[OSD([sQuery(id+"F18.wireOp",EDGE,"E28.right")])],"isStart":true})});
            var Q2;
            Q2=makeQuery(id+"F19.boolean.opBoolean","COPY",EDGE,{"derivedFrom":makeQuery(id+"F19.opExtrude","CAP_EDGE",EDGE,{"disambiguationData":[OSD([sQuery(id+"F18.wireOp",EDGE,"E28.top")])],"isStart":true})});
            var Q3;
            {var subQ0=sQuery(id+"F4.wireOp",EDGE,"E6.right");var subQ1=sQuery(id+"F4.wireOp",EDGE,"E6.bottom");var subQ2=sQuery(id+"F4.wireOp",EDGE,"E6.top");Q3=makeQuery(id+"F12.boolean.opBoolean","MERGE",EDGE,{"derivedFrom":[makeQuery(id+"F7.boolean.opBoolean","MERGE",EDGE,{"derivedFrom":[makeQuery(id+"F6.opExtrude","CAP_EDGE",EDGE,{"disambiguationData":[OSD([subQ0])],"isStart":false}),makeQuery(id+"F7.opExtrude","SWEPT_EDGE",EDGE,{"disambiguationData":[OSD([subQ2,subQ0]),TDD([makeQuery(id+"F6.opExtrude","CAP_VERTEX",VERTEX,{"disambiguationData":[OSD([subQ2,subQ0])],"isStart":false})])]})]}),makeQuery(id+"F12.opExtrude","SWEPT_EDGE",EDGE,{"disambiguationData":[OSD([subQ1,subQ0]),TDD([makeQuery(id+"F6.opExtrude","CAP_VERTEX",VERTEX,{"disambiguationData":[OSD([subQ1,subQ0])],"isStart":false})])]})]});}
            var Q4;
            {var subQ0=sQuery(id+"F4.wireOp",EDGE,"E6.right");var subQ1=sQuery(id+"F4.wireOp",EDGE,"E6.bottom");var subQ2=sQuery(id+"F4.wireOp",EDGE,"E6.top");Q4=makeQuery(id+"F12.boolean.opBoolean","MERGE",EDGE,{"derivedFrom":[makeQuery(id+"F7.boolean.opBoolean","MERGE",EDGE,{"derivedFrom":[makeQuery(id+"F6.opExtrude","CAP_EDGE",EDGE,{"disambiguationData":[OSD([subQ0])],"isStart":false}),makeQuery(id+"F7.opExtrude","SWEPT_EDGE",EDGE,{"disambiguationData":[OSD([subQ2,subQ0]),TDD([makeQuery(id+"F6.opExtrude","CAP_VERTEX",VERTEX,{"disambiguationData":[OSD([subQ2,subQ0])],"isStart":false})])]})]}),makeQuery(id+"F12.opExtrude","SWEPT_EDGE",EDGE,{"disambiguationData":[OSD([subQ1,subQ0]),TDD([makeQuery(id+"F6.opExtrude","CAP_VERTEX",VERTEX,{"disambiguationData":[OSD([subQ1,subQ0])],"isStart":false})])]})]});}
            fillet(context, id + "F22", {"entities" : qUnion([Q0, Q1, Q2, Q3, Q4]), "radius" : 3 * mm, "tangentPropagation" : true, "allowEdgeOverflow" : false});
        }
        {
            var Q0;
            Q0=qCreatedBy(makeId("Right.planeOp"),FACE);
            var sketch = newSketch(context, id + "F23", { "sketchPlane" : qUnion([Q0])});
            skLineSegment(sketch, "E36.bottom", {"start": v(3.28, 2.16) * mm, "end": v(-3.27, 2.16) * mm});
            skLineSegment(sketch, "E36.top", {"start": v(3.28, 0) * mm, "end": v(-3.27, 0) * mm});
            skLineSegment(sketch, "E36.left", {"start": v(3.28, 2.16) * mm, "end": v(3.28, 0) * mm});
            skLineSegment(sketch, "E36.right", {"start": v(-3.27, 2.16) * mm, "end": v(-3.27, 0) * mm});
            skPoint(sketch, "E36.middle", {"position": v(0, 1.08) * mm});
            skSolve(sketch);
        }
        {
            var Q0;
            Q0 = qSketchRegion(id + "F23", true);
            extrude(context, id + "F24", {"entities" : qUnion([Q0]), "operationType" : NewBodyOperationType.REMOVE, "endBound" : BoundingType.THROUGH_ALL, "oppositeDirection" : true, "depth" : 25 * mm, "offsetDistance" : 25 * mm, "hasSecondDirection" : true, "secondDirectionBound" : SecondDirectionBoundingType.THROUGH_ALL, "secondDirectionOppositeDirection" : false, "secondDirectionDepth" : 25 * mm});
        }
    });
